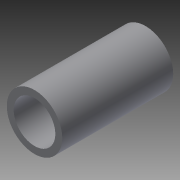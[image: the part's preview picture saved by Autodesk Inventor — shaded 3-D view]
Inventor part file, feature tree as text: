
AUTODESK INVENTOR PART (.ipt)
format: ipt  version: 2013 (Build 170138000, 138)  size: 78,848 bytes
history: native  units: in
note: dims shown in document units (in); Inventor stores cm internally (conversion verified against a paired STEP export)
features: extrude x1, sketch x1
ambient origin geometry x8: Origin, YZ Plane, XZ Plane, XY Plane, X Axis, Y Axis, Z Axis, Center Point
bodies: Solid1 (feature_tree)
feature tree (2):
  extrude  "Extrusion1"  Depth=0.5in
  sketch  "Sketch1"  dims[d0=0.375in d2=0.5in d3=1.0in d4=0.0in]
